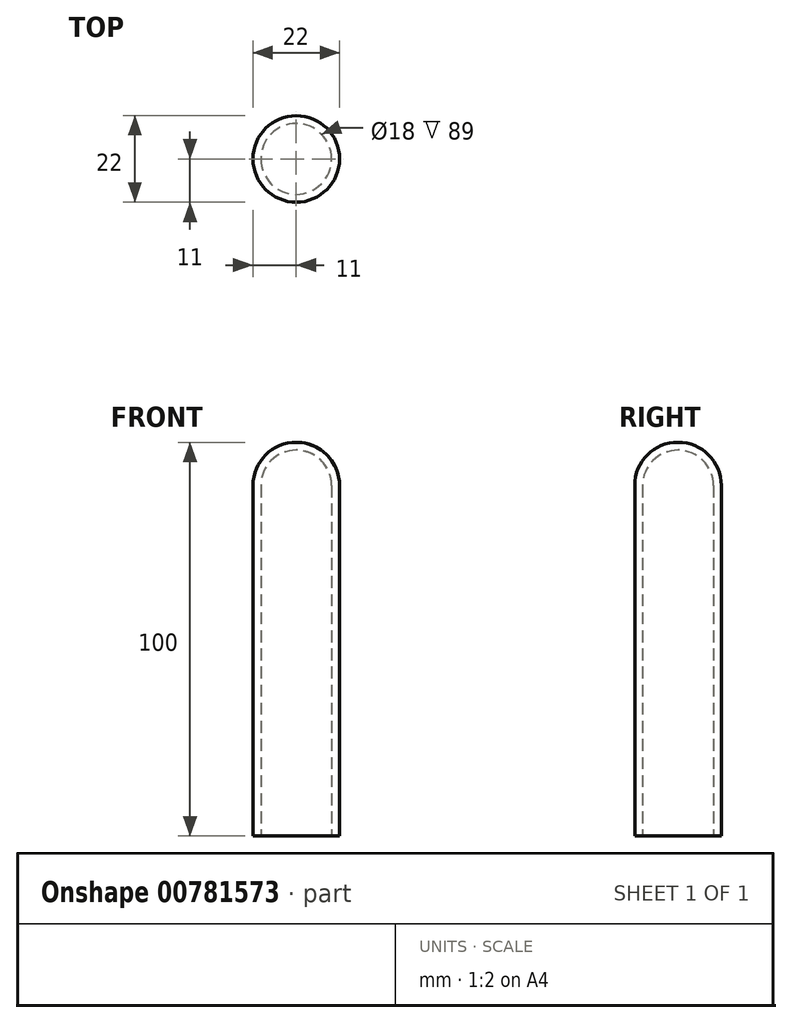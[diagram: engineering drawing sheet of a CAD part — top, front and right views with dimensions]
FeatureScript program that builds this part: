
annotation { "Feature Type Name" : "Feature", "Feature Type Description" : "" }
export const myFeature = defineFeature(function(context is Context, id is Id, definition is map)
    precondition{}
    {
        {
            var Q0;
            Q0=qCreatedBy(makeId("Top.planeOp"),FACE);
            var sketch = newSketch(context, id + "F0", { "sketchPlane" : qUnion([Q0])});
            skCircle(sketch, "E0", {"center": v(0, 0) * mm, "radius": 11 * mm});
            skSolve(sketch);
        }
        {
            var Q0;
            Q0 = qSketchRegion(id + "F0", true);
            extrude(context, id + "F1", {"entities" : qUnion([Q0]), "depth" : (89 + 11) * mm, "offsetDistance" : 25 * mm, "symmetric" : true});
        }
        {
            var Q0;
            Q0=makeQuery(id+"F1.opExtrude","CAP_EDGE",EDGE,{"disambiguationData":[OSD([sQuery(id+"F0.wireOp",EDGE,"E0")])],"isStart":false});
            fillet(context, id + "F2", {"entities" : qUnion([Q0]), "radius" : 11 * mm, "tangentPropagation" : true, "allowEdgeOverflow" : false});
        }
        {
            var Q0;
            Q0=makeQuery(id+"F1.opExtrude","CAP_FACE",FACE,{"disambiguationData":[OSD([sQuery(id+"F0.wireOp",EDGE,"E0")])],"isStart":true});
            shell(context, id + "F3", {"entities" : qUnion([Q0]), "thickness" : 2 * mm});
        }
    });
